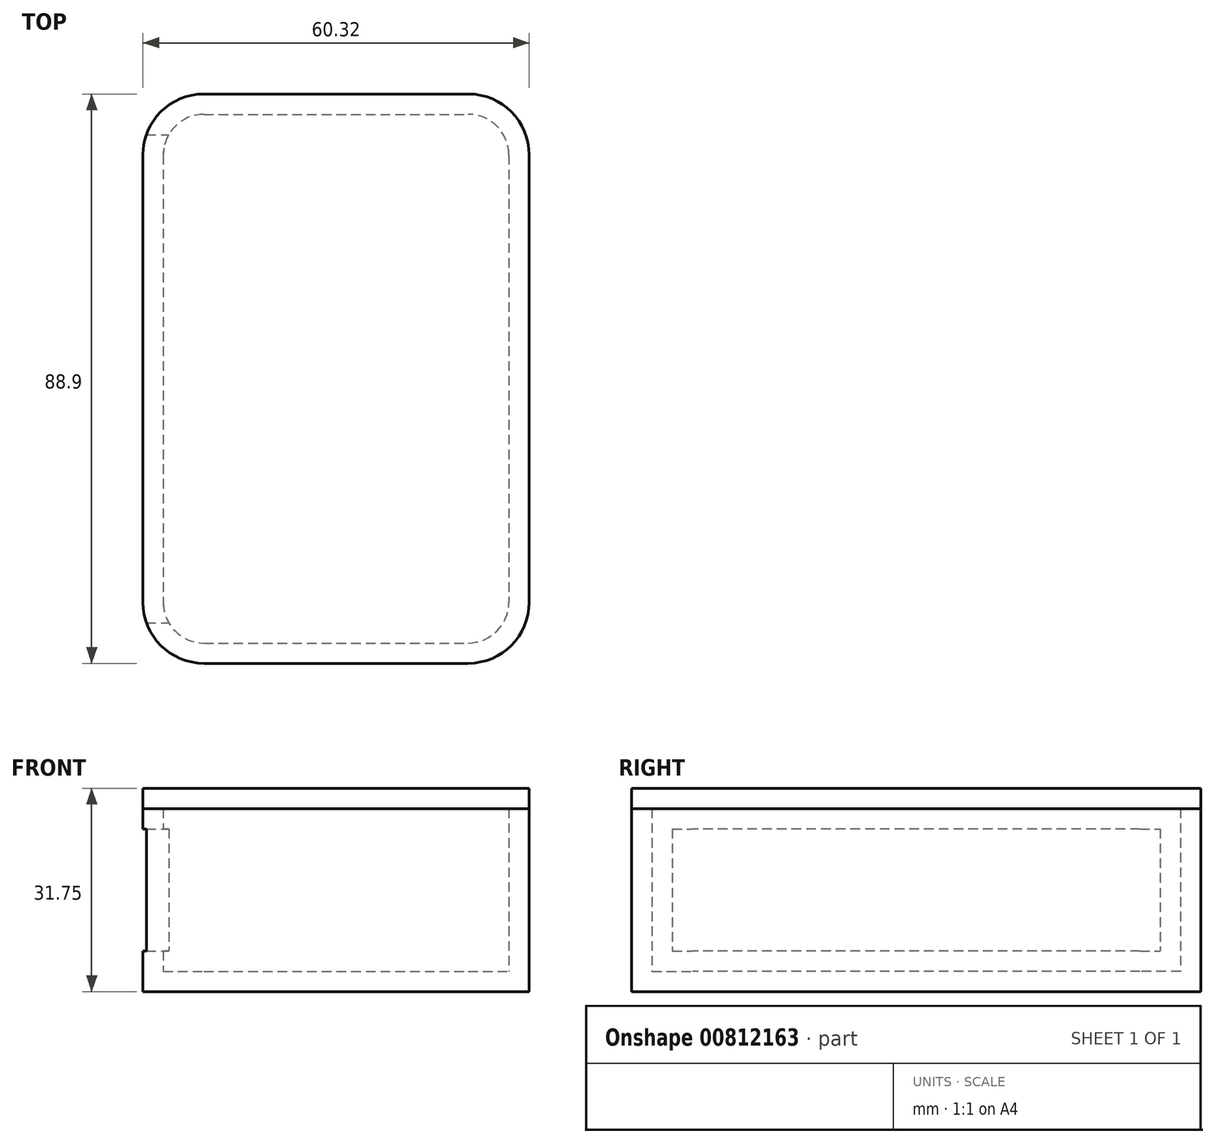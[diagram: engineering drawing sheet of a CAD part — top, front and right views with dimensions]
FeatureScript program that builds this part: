
annotation { "Feature Type Name" : "Feature", "Feature Type Description" : "" }
export const myFeature = defineFeature(function(context is Context, id is Id, definition is map)
    precondition{}
    {
        {
            var Q0;
            Q0=qCreatedBy(makeId("Top.planeOp"),FACE);
            var sketch = newSketch(context, id + "F0", { "sketchPlane" : qUnion([Q0])});
            skLineSegment(sketch, "E0.bottom", {"start": v(20.64, -41.28) * mm, "end": v(-20.64, -41.28) * mm});
            skLineSegment(sketch, "E0.top", {"start": v(20.64, 41.28) * mm, "end": v(-20.64, 41.28) * mm});
            skLineSegment(sketch, "E0.left", {"start": v(26.99, -34.93) * mm, "end": v(26.99, 34.93) * mm});
            skLineSegment(sketch, "E0.right", {"start": v(-26.99, -34.92) * mm, "end": v(-26.99, 34.92) * mm});
            skPoint(sketch, "E0.middle", {"position": v(0, 0) * mm});
            skPoint(sketch, "E1.visualSharp", {"position": v(26.99, 41.28) * mm});
            skArc(sketch, "E1.filletArc", {"start": v(26.99, 34.93) * mm, "mid": v(25.13, 39.42) * mm, "end": v(20.64, 41.28) * mm});
            skPoint(sketch, "E2.visualSharp", {"position": v(26.99, -41.28) * mm});
            skArc(sketch, "E2.filletArc", {"start": v(20.64, -41.28) * mm, "mid": v(25.13, -39.42) * mm, "end": v(26.99, -34.93) * mm});
            skPoint(sketch, "E3.visualSharp", {"position": v(-26.99, -41.28) * mm});
            skArc(sketch, "E3.filletArc", {"start": v(-26.99, -34.92) * mm, "mid": v(-25.13, -39.42) * mm, "end": v(-20.64, -41.28) * mm});
            skPoint(sketch, "E4.visualSharp", {"position": v(-26.99, 41.28) * mm});
            skArc(sketch, "E4.filletArc", {"start": v(-20.64, 41.28) * mm, "mid": v(-25.13, 39.42) * mm, "end": v(-26.99, 34.92) * mm});
            skLineSegment(sketch, "E5.bottom", {"start": v(20.64, -44.45) * mm, "end": v(-20.64, -44.45) * mm});
            skLineSegment(sketch, "E5.top", {"start": v(20.64, 44.45) * mm, "end": v(-20.64, 44.45) * mm});
            skLineSegment(sketch, "E5.left", {"start": v(30.16, -34.93) * mm, "end": v(30.16, 34.93) * mm});
            skLineSegment(sketch, "E5.right", {"start": v(-30.16, -34.93) * mm, "end": v(-30.16, 34.93) * mm});
            skPoint(sketch, "E6.visualSharp", {"position": v(30.16, 44.45) * mm});
            skArc(sketch, "E6.filletArc", {"start": v(30.16, 34.93) * mm, "mid": v(27.37, 41.66) * mm, "end": v(20.64, 44.45) * mm});
            skPoint(sketch, "E7.visualSharp", {"position": v(30.16, -44.45) * mm});
            skArc(sketch, "E7.filletArc", {"start": v(20.64, -44.45) * mm, "mid": v(27.37, -41.66) * mm, "end": v(30.16, -34.93) * mm});
            skPoint(sketch, "E8.visualSharp", {"position": v(-30.16, -44.45) * mm});
            skArc(sketch, "E8.filletArc", {"start": v(-30.16, -34.93) * mm, "mid": v(-27.37, -41.66) * mm, "end": v(-20.64, -44.45) * mm});
            skPoint(sketch, "E9.visualSharp", {"position": v(-30.16, 44.45) * mm});
            skArc(sketch, "E9.filletArc", {"start": v(-20.64, 44.45) * mm, "mid": v(-27.37, 41.66) * mm, "end": v(-30.16, 34.93) * mm});
            skSolve(sketch);
        }
        {
            var Q0;
            Q0=makeQuery(id+"F0.imprint","IMPRINT",FACE,{"disambiguationData":[TD([[makeQuery(id+"F0.imprint","IMPRINT",EDGE,{"derivedFrom":sQuery(id+"F0.wireOp",EDGE,"E0.bottom")}),-1.0]])]});
            var Q1;
            Q1=makeQuery(id+"F0.imprint","IMPRINT",FACE,{"disambiguationData":[TD([[makeQuery(id+"F0.imprint","IMPRINT",EDGE,{"derivedFrom":sQuery(id+"F0.wireOp",EDGE,"E0.bottom")}),1.0]])]});
            extrude(context, id + "F1", {"entities" : qUnion([Q0, Q1]), "depth" : 3.17 * mm, "offsetDistance" : 25.4 * mm});
        }
        {
            var Q0;
            Q0=makeQuery(id+"F0.imprint","IMPRINT",FACE,{"disambiguationData":[TD([[makeQuery(id+"F0.imprint","IMPRINT",EDGE,{"derivedFrom":sQuery(id+"F0.wireOp",EDGE,"E0.bottom")}),1.0]])]});
            extrude(context, id + "F2", {"entities" : qUnion([Q0]), "operationType" : NewBodyOperationType.ADD, "depth" : 28.57 * mm, "offsetDistance" : 25.4 * mm});
        }
        {
            var Q0;
            Q0=makeQuery(id+"F0.imprint","IMPRINT",FACE,{"disambiguationData":[TD([[makeQuery(id+"F0.imprint","IMPRINT",EDGE,{"derivedFrom":sQuery(id+"F0.wireOp",EDGE,"E0.bottom")}),-1.0]])]});
            var Q1;
            Q1=makeQuery(id+"F0.imprint","IMPRINT",FACE,{"disambiguationData":[TD([[makeQuery(id+"F0.imprint","IMPRINT",EDGE,{"derivedFrom":sQuery(id+"F0.wireOp",EDGE,"E0.bottom")}),1.0]])]});
            extrude(context, id + "F3", {"entities" : qUnion([Q0, Q1]), "depth" : 31.75 * mm, "offsetDistance" : 25.4 * mm, "hasSecondDirection" : true, "secondDirectionOppositeDirection" : false, "secondDirectionDepth" : 28.57 * mm});
        }
        {
            var Q0;
            Q0=qCreatedBy(makeId("Right.planeOp"),FACE);
            var sketch = newSketch(context, id + "F4", { "sketchPlane" : qUnion([Q0])});
            skLineSegment(sketch, "E10.bottom", {"start": v(-38.1, 6.35) * mm, "end": v(38.1, 6.35) * mm});
            skLineSegment(sketch, "E10.top", {"start": v(-38.1, 25.4) * mm, "end": v(38.1, 25.4) * mm});
            skLineSegment(sketch, "E10.left", {"start": v(-38.1, 6.35) * mm, "end": v(-38.1, 25.4) * mm});
            skLineSegment(sketch, "E10.right", {"start": v(38.1, 6.35) * mm, "end": v(38.1, 25.4) * mm});
            skPoint(sketch, "E10.middle", {"position": v(0, 15.88) * mm});
            skSolve(sketch);
        }
        {
            var Q0;
            Q0=makeQuery(id+"F4.imprint","IMPRINT",FACE,{"disambiguationData":[TD([[makeQuery(id+"F4.imprint","IMPRINT",EDGE,{"derivedFrom":sQuery(id+"F4.wireOp",EDGE,"E10.bottom")}),1.0]])]});
            extrude(context, id + "F5", {"entities" : qUnion([Q0]), "operationType" : NewBodyOperationType.REMOVE, "oppositeDirection" : true, "depth" : 50.8 * mm, "offsetDistance" : 25.4 * mm});
        }
    });
